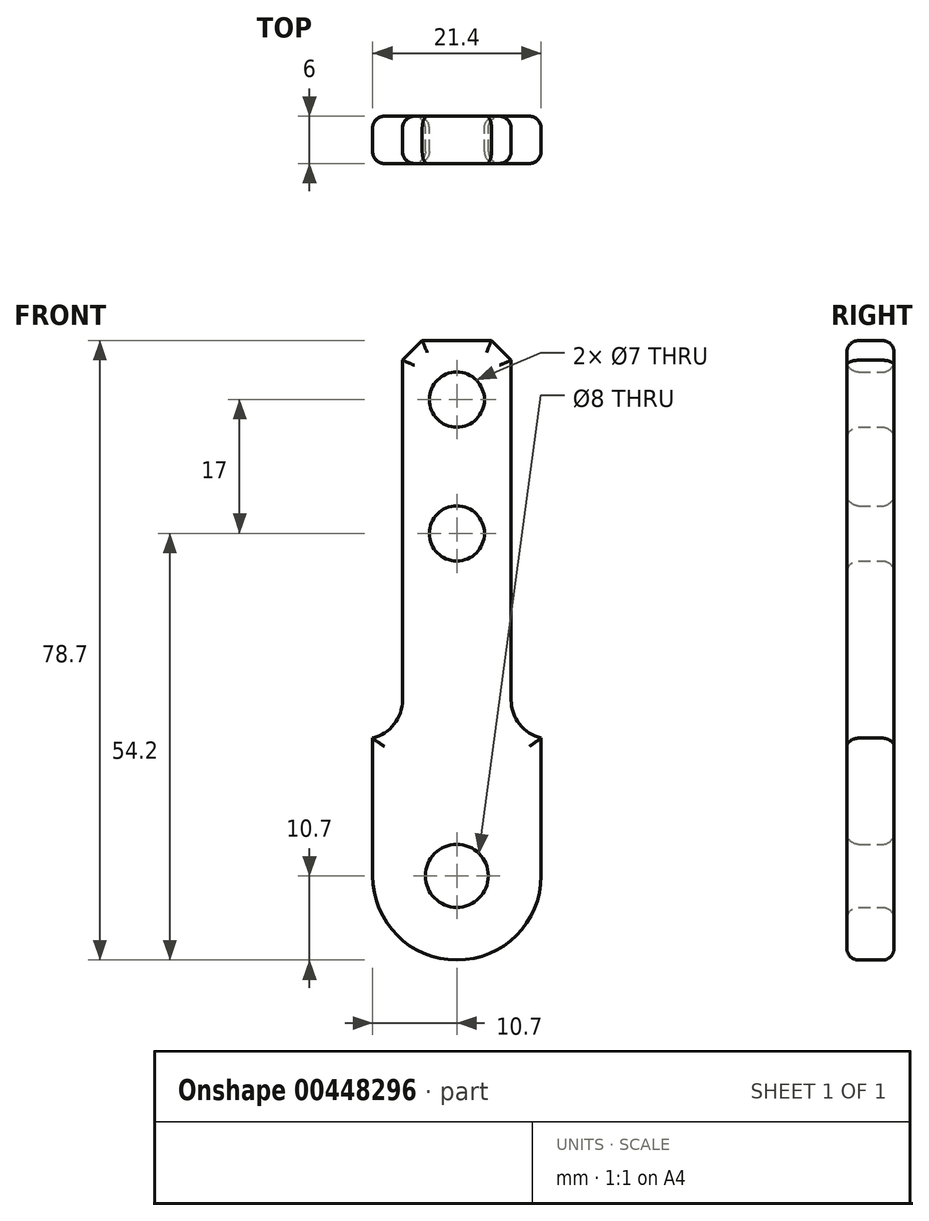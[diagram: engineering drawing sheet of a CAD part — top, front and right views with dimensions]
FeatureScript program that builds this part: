
annotation { "Feature Type Name" : "Feature", "Feature Type Description" : "" }
export const myFeature = defineFeature(function(context is Context, id is Id, definition is map)
    precondition{}
    {
        {
            var Q0;
            Q0=qCreatedBy(makeId("Front.planeOp"),FACE);
            var sketch = newSketch(context, id + "F0", { "sketchPlane" : qUnion([Q0])});
            skCircle(sketch, "E0", {"center": v(0, 0) * mm, "radius": 4 * mm});
            skCircle(sketch, "E1", {"center": v(0, 43.5) * mm, "radius": 3.5 * mm});
            skCircle(sketch, "E2", {"center": v(0, 60.5) * mm, "radius": 3.5 * mm});
            skArc(sketch, "E3", {"start": v(10.7, 0) * mm, "mid": v(0, -10.7) * mm, "end": v(-10.7, 0) * mm});
            skLineSegment(sketch, "E4", {"start": v(10.7, 0) * mm, "end": v(10.7, 17.5) * mm});
            skLineSegment(sketch, "E5", {"start": v(0, 0) * mm, "end": v(0, -10.7) * mm});
            skLineSegment(sketch, "E6.MirrorCS", {"start": v(-10.7, 0) * mm, "end": v(-10.7, 17.5) * mm});
            skLineSegment(sketch, "E7", {"start": v(10.7, 17.5) * mm, "end": v(6.9, 17.5) * mm});
            skLineSegment(sketch, "E8", {"start": v(6.9, 17.5) * mm, "end": v(6.9, 68) * mm});
            skLineSegment(sketch, "E9.MirrorCS", {"start": v(-6.9, 17.5) * mm, "end": v(-6.9, 68) * mm});
            skLineSegment(sketch, "E10.MirrorCS", {"start": v(-10.7, 17.5) * mm, "end": v(-6.9, 17.5) * mm});
            skLineSegment(sketch, "E11", {"start": v(-6.9, 68) * mm, "end": v(6.9, 68) * mm});
            skSolve(sketch);
        }
        {
            var Q0;
            Q0=makeQuery(id+"F0.imprint","IMPRINT",FACE,{"disambiguationData":[TD([[makeQuery(id+"F0.imprint","IMPRINT",EDGE,{"derivedFrom":sQuery(id+"F0.wireOp",EDGE,"E0")}),-1.0]])]});
            extrude(context, id + "F1", {"entities" : qUnion([Q0]), "endBound" : BoundingType.SYMMETRIC, "depth" : 6 * mm});
        }
        {
            var Q0;
            Q0=makeQuery(id+"F1.opExtrude","SWEPT_EDGE",EDGE,{"disambiguationData":[OSD([sQuery(id+"F0.wireOp",EDGE,"E9.MirrorCS"),sQuery(id+"F0.wireOp",EDGE,"E10.MirrorCS")])]});
            var Q1;
            Q1=makeQuery(id+"F1.opExtrude","SWEPT_EDGE",EDGE,{"disambiguationData":[OSD([sQuery(id+"F0.wireOp",EDGE,"E7"),sQuery(id+"F0.wireOp",EDGE,"E8")])]});
            fillet(context, id + "F2", {"entities" : qUnion([Q0, Q1]), "radius" : 5 * mm, "tangentPropagation" : true, "allowEdgeOverflow" : false});
        }
        {
            var Q0;
            Q0=makeQuery(id+"F1.opExtrude","SWEPT_EDGE",EDGE,{"disambiguationData":[OSD([sQuery(id+"F0.wireOp",EDGE,"E9.MirrorCS"),sQuery(id+"F0.wireOp",EDGE,"E11")])]});
            var Q1;
            Q1=makeQuery(id+"F1.opExtrude","SWEPT_EDGE",EDGE,{"disambiguationData":[OSD([sQuery(id+"F0.wireOp",EDGE,"E8"),sQuery(id+"F0.wireOp",EDGE,"E11")])]});
            chamfer(context, id + "F3", {"entities" : qUnion([Q0, Q1]), "width" : 2.5 * mm, "tangentPropagation" : true});
        }
        {
            var Q0;
            Q0=makeQuery(id+"F1.opExtrude","CAP_FACE",FACE,{"disambiguationData":[OSD([sQuery(id+"F0.wireOp",EDGE,"E0"),sQuery(id+"F0.wireOp",EDGE,"E1"),sQuery(id+"F0.wireOp",EDGE,"E2"),sQuery(id+"F0.wireOp",EDGE,"E3"),sQuery(id+"F0.wireOp",EDGE,"E4"),sQuery(id+"F0.wireOp",EDGE,"E6.MirrorCS"),sQuery(id+"F0.wireOp",EDGE,"E7"),sQuery(id+"F0.wireOp",EDGE,"E8"),sQuery(id+"F0.wireOp",EDGE,"E9.MirrorCS"),sQuery(id+"F0.wireOp",EDGE,"E10.MirrorCS"),sQuery(id+"F0.wireOp",EDGE,"E11")])],"isStart":false});
            var Q1;
            Q1=makeQuery(id+"F1.opExtrude","CAP_FACE",FACE,{"disambiguationData":[OSD([sQuery(id+"F0.wireOp",EDGE,"E0"),sQuery(id+"F0.wireOp",EDGE,"E1"),sQuery(id+"F0.wireOp",EDGE,"E2"),sQuery(id+"F0.wireOp",EDGE,"E3"),sQuery(id+"F0.wireOp",EDGE,"E4"),sQuery(id+"F0.wireOp",EDGE,"E6.MirrorCS"),sQuery(id+"F0.wireOp",EDGE,"E7"),sQuery(id+"F0.wireOp",EDGE,"E8"),sQuery(id+"F0.wireOp",EDGE,"E9.MirrorCS"),sQuery(id+"F0.wireOp",EDGE,"E10.MirrorCS"),sQuery(id+"F0.wireOp",EDGE,"E11")])],"isStart":true});
            fillet(context, id + "F4", {"entities" : qUnion([Q0, Q1]), "radius" : 1.5 * mm, "tangentPropagation" : true, "allowEdgeOverflow" : false});
        }
    });
